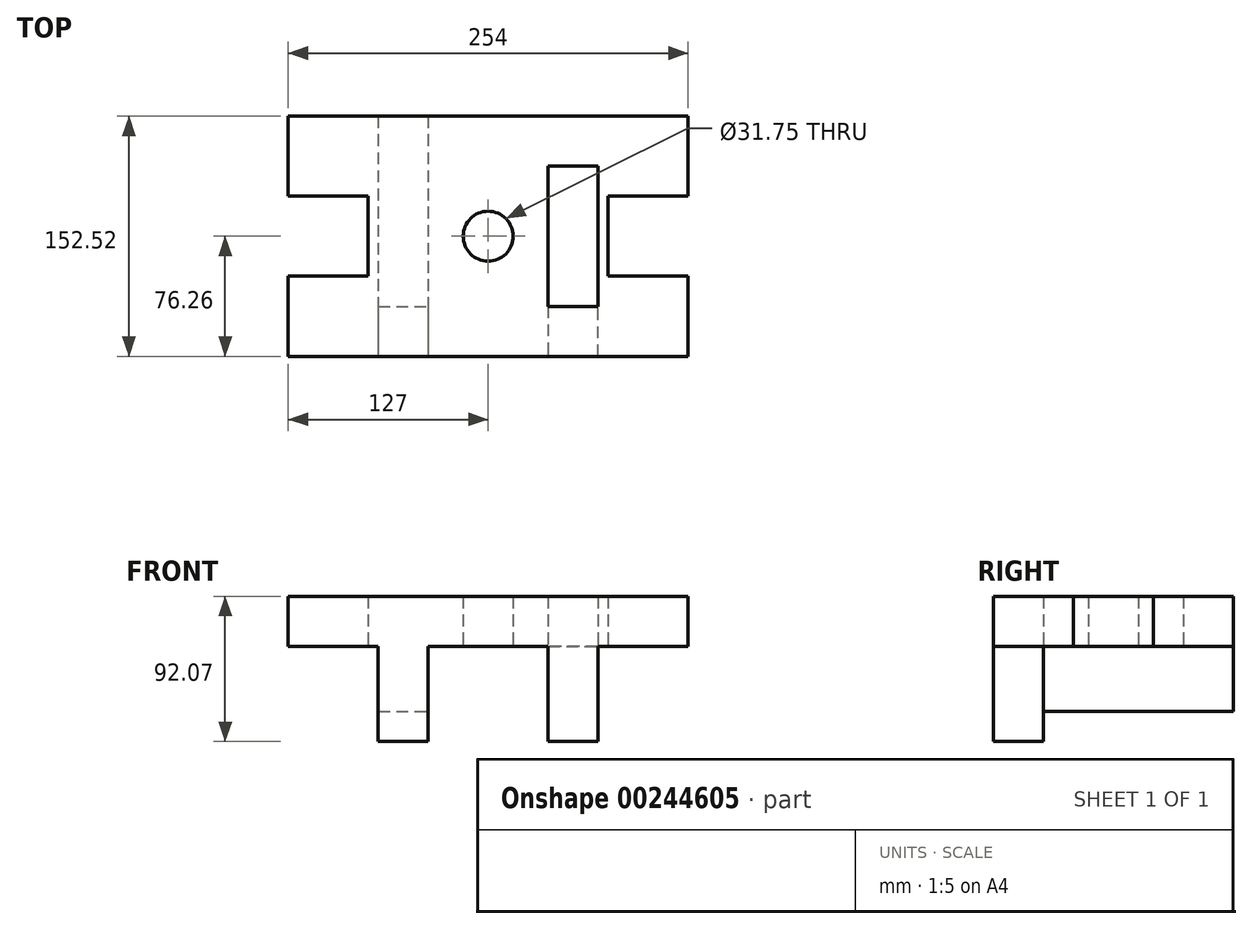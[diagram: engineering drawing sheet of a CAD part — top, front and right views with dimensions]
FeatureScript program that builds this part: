
annotation { "Feature Type Name" : "Feature", "Feature Type Description" : "" }
export const myFeature = defineFeature(function(context is Context, id is Id, definition is map)
    precondition{}
    {
        {
            var Q0;
            Q0=qCreatedBy(makeId("Top.planeOp"),FACE);
            var sketch = newSketch(context, id + "F0", { "sketchPlane" : qUnion([Q0])});
            skLineSegment(sketch, "E0.bottom", {"start": v(127, 76.26) * mm, "end": v(-127, 76.26) * mm});
            skLineSegment(sketch, "E0.top", {"start": v(127, -76.26) * mm, "end": v(-127, -76.26) * mm});
            skLineSegment(sketch, "E0.left", {"start": v(127, 76.26) * mm, "end": v(127, 25.46) * mm});
            skLineSegment(sketch, "E0.right", {"start": v(-127, 76.26) * mm, "end": v(-127, 25.46) * mm});
            skPoint(sketch, "E0.middle", {"position": v(0, 0) * mm});
            skLineSegment(sketch, "E1.bottom", {"start": v(-127, 25.46) * mm, "end": v(-76.2, 25.46) * mm});
            skLineSegment(sketch, "E1.top", {"start": v(-127, -25.34) * mm, "end": v(-76.2, -25.34) * mm});
            skLineSegment(sketch, "E1.right", {"start": v(-76.2, 25.46) * mm, "end": v(-76.2, -25.34) * mm});
            skLineSegment(sketch, "E2.bottom", {"start": v(127, 25.46) * mm, "end": v(76.2, 25.46) * mm});
            skLineSegment(sketch, "E2.top", {"start": v(127, -25.34) * mm, "end": v(76.2, -25.34) * mm});
            skLineSegment(sketch, "E2.right", {"start": v(76.2, 25.46) * mm, "end": v(76.2, -25.34) * mm});
            skLineSegment(sketch, "E3.trimOffspring", {"start": v(-127, -25.34) * mm, "end": v(-127, -76.26) * mm});
            skLineSegment(sketch, "E4.trimOffspring", {"start": v(127, -25.34) * mm, "end": v(127, -76.26) * mm});
            skLineSegment(sketch, "E5.bottom", {"start": v(-38.1, 76.26) * mm, "end": v(38.1, 76.26) * mm});
            skLineSegment(sketch, "E5.top", {"start": v(-38.1, -76.26) * mm, "end": v(38.1, -76.26) * mm});
            skLineSegment(sketch, "E5.left", {"start": v(-38.1, 76.26) * mm, "end": v(-38.1, -76.26) * mm});
            skLineSegment(sketch, "E5.right", {"start": v(38.1, 76.26) * mm, "end": v(38.1, -76.26) * mm});
            skLineSegment(sketch, "E6.bottom", {"start": v(-38.1, 76.26) * mm, "end": v(-69.85, 76.26) * mm});
            skLineSegment(sketch, "E6.top", {"start": v(-38.1, -76.26) * mm, "end": v(-69.85, -76.26) * mm});
            skLineSegment(sketch, "E6.right", {"start": v(-69.85, 76.26) * mm, "end": v(-69.85, -76.26) * mm});
            skLineSegment(sketch, "E7.bottom", {"start": v(38.1, -76.26) * mm, "end": v(69.85, -76.26) * mm});
            skLineSegment(sketch, "E7.top", {"start": v(38.1, 76.26) * mm, "end": v(69.85, 76.26) * mm});
            skLineSegment(sketch, "E7.left", {"start": v(38.1, -76.26) * mm, "end": v(38.1, 76.26) * mm});
            skLineSegment(sketch, "E7.right", {"start": v(69.85, -76.26) * mm, "end": v(69.85, 76.26) * mm});
            skLineSegment(sketch, "E8.bottom", {"start": v(-69.85, 76.26) * mm, "end": v(-38.1, 76.26) * mm});
            skLineSegment(sketch, "E8.top", {"start": v(-69.85, 44.5) * mm, "end": v(-38.1, 44.5) * mm});
            skLineSegment(sketch, "E8.left", {"start": v(-69.85, 76.26) * mm, "end": v(-69.85, 44.5) * mm});
            skLineSegment(sketch, "E8.right", {"start": v(-38.1, 76.26) * mm, "end": v(-38.1, 44.5) * mm});
            skLineSegment(sketch, "E9.top", {"start": v(38.1, 44.5) * mm, "end": v(69.85, 44.5) * mm});
            skLineSegment(sketch, "E9.left", {"start": v(38.1, 76.26) * mm, "end": v(38.1, 44.5) * mm});
            skLineSegment(sketch, "E9.right", {"start": v(69.85, 76.26) * mm, "end": v(69.85, 44.5) * mm});
            skLineSegment(sketch, "E10.bottom", {"start": v(-69.85, -44.5) * mm, "end": v(-38.1, -44.5) * mm});
            skLineSegment(sketch, "E10.top", {"start": v(-69.85, -76.26) * mm, "end": v(-38.1, -76.26) * mm});
            skLineSegment(sketch, "E10.left", {"start": v(-69.85, -44.5) * mm, "end": v(-69.85, -76.26) * mm});
            skLineSegment(sketch, "E10.right", {"start": v(-38.1, -44.5) * mm, "end": v(-38.1, -76.26) * mm});
            skLineSegment(sketch, "E11.bottom", {"start": v(38.1, -44.5) * mm, "end": v(69.85, -44.5) * mm});
            skLineSegment(sketch, "E11.left", {"start": v(38.1, -44.5) * mm, "end": v(38.1, -76.26) * mm});
            skLineSegment(sketch, "E11.right", {"start": v(69.85, -44.5) * mm, "end": v(69.85, -76.26) * mm});
            skCircle(sketch, "E12", {"center": v(0, 0) * mm, "radius": 15.88 * mm});
            skSolve(sketch);
        }
        {
            var Q0;
            Q0 = qSketchRegion(id + "F0", true);
            var Q1;
            Q1=makeQuery(id+"F0.imprint","IMPRINT",FACE,{"disambiguationData":[TD([[makeQuery(id+"F0.imprint","IMPRINT",EDGE,{"derivedFrom":sQuery(id+"F0.wireOp",EDGE,"E5.left")}),-1.0]])]});
            var Q2;
            Q2=makeQuery(id+"F0.imprint","IMPRINT",FACE,{"disambiguationData":[TD([[makeQuery(id+"F0.imprint","IMPRINT",EDGE,{"derivedFrom":sQuery(id+"F0.wireOp",EDGE,"E7.left")}),-1.0]])]});
            extrude(context, id + "F1", {"entities" : qUnion([Q0, Q1, Q2]), "depth" : 31.75 * mm});
        }
        {
            var Q0;
            Q0=makeQuery(id+"F0.imprint","IMPRINT",FACE,{"disambiguationData":[TD([[makeQuery(id+"F0.imprint","IMPRINT",EDGE,{"derivedFrom":sQuery(id+"F0.wireOp",EDGE,"E10.bottom")}),-1.0]])]});
            var Q1;
            Q1=makeQuery(id+"F0.imprint","IMPRINT",FACE,{"disambiguationData":[TD([[makeQuery(id+"F0.imprint","IMPRINT",EDGE,{"derivedFrom":sQuery(id+"F0.wireOp",EDGE,"E5.left")}),-1.0]])]});
            var Q2;
            Q2=makeQuery(id+"F0.imprint","IMPRINT",FACE,{"disambiguationData":[TD([[makeQuery(id+"F0.imprint","IMPRINT",EDGE,{"derivedFrom":sQuery(id+"F0.wireOp",EDGE,"E8.bottom")}),-1.0]])]});
            var Q3;
            Q3=makeQuery(id+"F0.imprint","IMPRINT",FACE,{"disambiguationData":[TD([[makeQuery(id+"F0.imprint","IMPRINT",EDGE,{"derivedFrom":sQuery(id+"F0.wireOp",EDGE,"E5.bottom")}),-1.0]])]});
            var Q4;
            Q4=makeQuery(id+"F0.imprint","IMPRINT",FACE,{"disambiguationData":[TD([[makeQuery(id+"F0.imprint","IMPRINT",EDGE,{"derivedFrom":sQuery(id+"F0.wireOp",EDGE,"E7.top")}),-1.0]])]});
            var Q5;
            Q5=makeQuery(id+"F0.imprint","IMPRINT",FACE,{"disambiguationData":[TD([[makeQuery(id+"F0.imprint","IMPRINT",EDGE,{"derivedFrom":sQuery(id+"F0.wireOp",EDGE,"E7.left")}),-1.0]])]});
            var Q6;
            Q6=makeQuery(id+"F0.imprint","IMPRINT",FACE,{"disambiguationData":[TD([[makeQuery(id+"F0.imprint","IMPRINT",EDGE,{"derivedFrom":sQuery(id+"F0.wireOp",EDGE,"E11.bottom")}),-1.0]])]});
            extrude(context, id + "F2", {"entities" : qUnion([Q0, Q1, Q2, Q3, Q4, Q5, Q6]), "operationType" : NewBodyOperationType.ADD, "oppositeDirection" : true, "depth" : 22.22 * mm});
        }
        {
            var Q0;
            Q0=makeQuery(id+"F0.imprint","IMPRINT",FACE,{"disambiguationData":[TD([[makeQuery(id+"F0.imprint","IMPRINT",EDGE,{"derivedFrom":sQuery(id+"F0.wireOp",EDGE,"E8.bottom")}),-1.0]])]});
            var Q1;
            Q1=makeQuery(id+"F0.imprint","IMPRINT",FACE,{"disambiguationData":[TD([[makeQuery(id+"F0.imprint","IMPRINT",EDGE,{"derivedFrom":sQuery(id+"F0.wireOp",EDGE,"E10.bottom")}),-1.0]])]});
            var Q2;
            Q2=makeQuery(id+"F0.imprint","IMPRINT",FACE,{"disambiguationData":[TD([[makeQuery(id+"F0.imprint","IMPRINT",EDGE,{"derivedFrom":sQuery(id+"F0.wireOp",EDGE,"E11.bottom")}),-1.0]])]});
            var Q3;
            Q3=makeQuery(id+"F0.imprint","IMPRINT",FACE,{"disambiguationData":[TD([[makeQuery(id+"F0.imprint","IMPRINT",EDGE,{"derivedFrom":sQuery(id+"F0.wireOp",EDGE,"E7.top")}),-1.0]])]});
            var Q4;
            Q4=makeQuery(id+"F0.imprint","IMPRINT",FACE,{"disambiguationData":[TD([[makeQuery(id+"F0.imprint","IMPRINT",EDGE,{"derivedFrom":sQuery(id+"F0.wireOp",EDGE,"E5.left")}),-1.0]])]});
            var Q5;
            Q5=makeQuery(id+"F0.imprint","IMPRINT",FACE,{"disambiguationData":[TD([[makeQuery(id+"F0.imprint","IMPRINT",EDGE,{"derivedFrom":sQuery(id+"F0.wireOp",EDGE,"E7.left")}),-1.0]])]});
            extrude(context, id + "F3", {"entities" : qUnion([Q0, Q1, Q2, Q3, Q4, Q5]), "operationType" : NewBodyOperationType.ADD, "oppositeDirection" : true, "depth" : 41.27 * mm});
        }
        {
            var Q0;
            Q0=makeQuery(id+"F0.imprint","IMPRINT",FACE,{"disambiguationData":[TD([[makeQuery(id+"F0.imprint","IMPRINT",EDGE,{"derivedFrom":sQuery(id+"F0.wireOp",EDGE,"E8.bottom")}),-1.0]])]});
            var Q1;
            Q1=makeQuery(id+"F0.imprint","IMPRINT",FACE,{"disambiguationData":[TD([[makeQuery(id+"F0.imprint","IMPRINT",EDGE,{"derivedFrom":sQuery(id+"F0.wireOp",EDGE,"E10.bottom")}),-1.0]])]});
            var Q2;
            Q2=makeQuery(id+"F0.imprint","IMPRINT",FACE,{"disambiguationData":[TD([[makeQuery(id+"F0.imprint","IMPRINT",EDGE,{"derivedFrom":sQuery(id+"F0.wireOp",EDGE,"E11.bottom")}),-1.0]])]});
            var Q3;
            Q3=makeQuery(id+"F0.imprint","IMPRINT",FACE,{"disambiguationData":[TD([[makeQuery(id+"F0.imprint","IMPRINT",EDGE,{"derivedFrom":sQuery(id+"F0.wireOp",EDGE,"E7.top")}),-1.0]])]});
            extrude(context, id + "F4", {"entities" : qUnion([Q0, Q1, Q2, Q3]), "operationType" : NewBodyOperationType.ADD, "oppositeDirection" : true, "depth" : 60.32 * mm});
        }
    });
